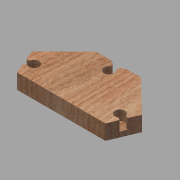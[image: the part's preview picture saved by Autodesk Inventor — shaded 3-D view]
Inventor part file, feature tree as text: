
AUTODESK INVENTOR PART (.ipt)
format: ipt  version: 2014 (Build 180170000, 170)  size: 153,600 bytes
history: native  units: mm
features: reference x4, extrude x2, sketch x2
ambient origin geometry x8: Origin, YZ Plane, XZ Plane, XY Plane, X Axis, Y Axis, Z Axis, Center Point
bodies: Solid1 (feature_tree)
feature tree (8):
  extrude  "Extrusion1"  Depth=226.0mm
  extrude  "Extrusion2"  Depth=20.0mm
  sketch  "Sketch1"  dims[d0=113.0mm d1=226.0mm]
  sketch  "Sketch2"  dims[d2=110.0mm d3=26.0mm d5=26.0mm d14=20.0mm d17=20.0mm d18=20.0mm d19=25.0mm d20=20.0mm d21=25.0mm d22=25.0mm d23=25.0mm d24=22.0mm d25=30.0mm d26=0.0mm d27=20.0mm d28=0.0mm]
  reference  "Reference1"
  reference  "Reference2"
  reference  "Reference3"
  reference  "Reference4"
